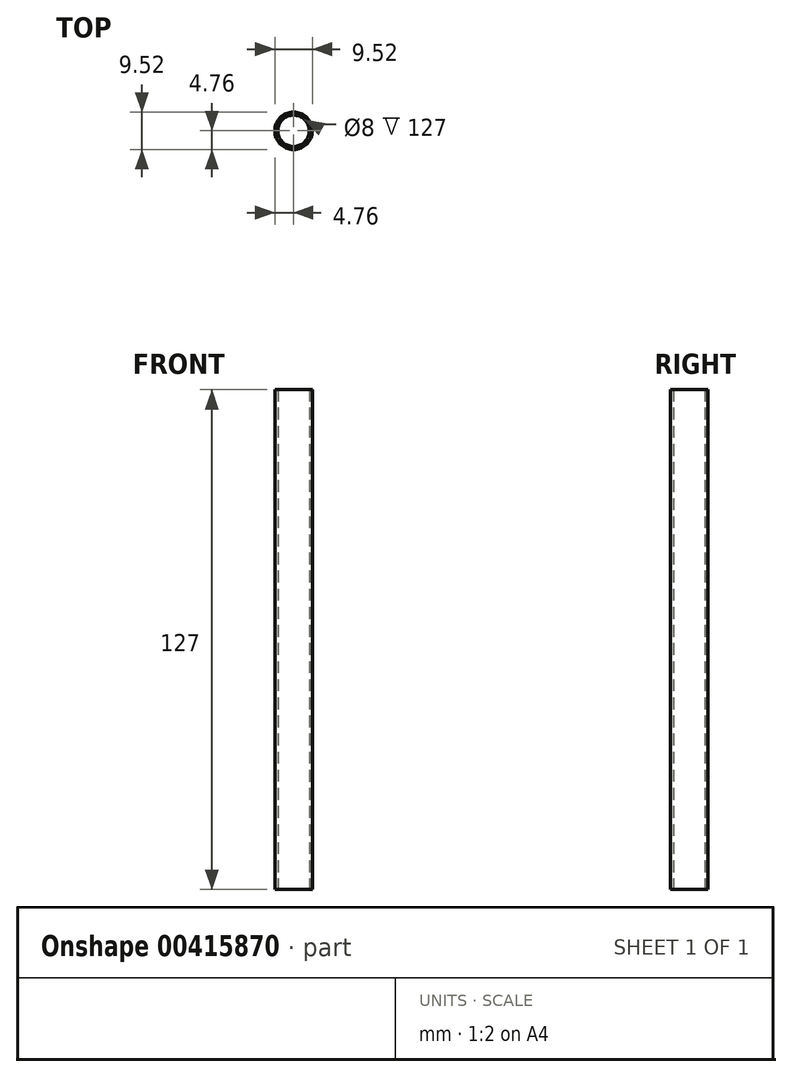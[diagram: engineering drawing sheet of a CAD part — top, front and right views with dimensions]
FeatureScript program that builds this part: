
annotation { "Feature Type Name" : "Feature", "Feature Type Description" : "" }
export const myFeature = defineFeature(function(context is Context, id is Id, definition is map)
    precondition{}
    {
        {
            var Q0;
            Q0=qCreatedBy(makeId("Top.planeOp"),FACE);
            var sketch = newSketch(context, id + "F0", { "sketchPlane" : qUnion([Q0])});
            skCircle(sketch, "E0", {"center": v(0, 0) * mm, "radius": 4.76 * mm});
            skCircle(sketch, "E1.0", {"center": v(0, 0) * mm, "radius": 4 * mm});
            skSolve(sketch);
        }
        {
            var Q0;
            Q0 = qSketchRegion(id + "F0", true);
            extrude(context, id + "F1", {"entities" : qUnion([Q0]), "depth" : 127 * mm, "offsetDistance" : 25.4 * mm});
        }
    });
